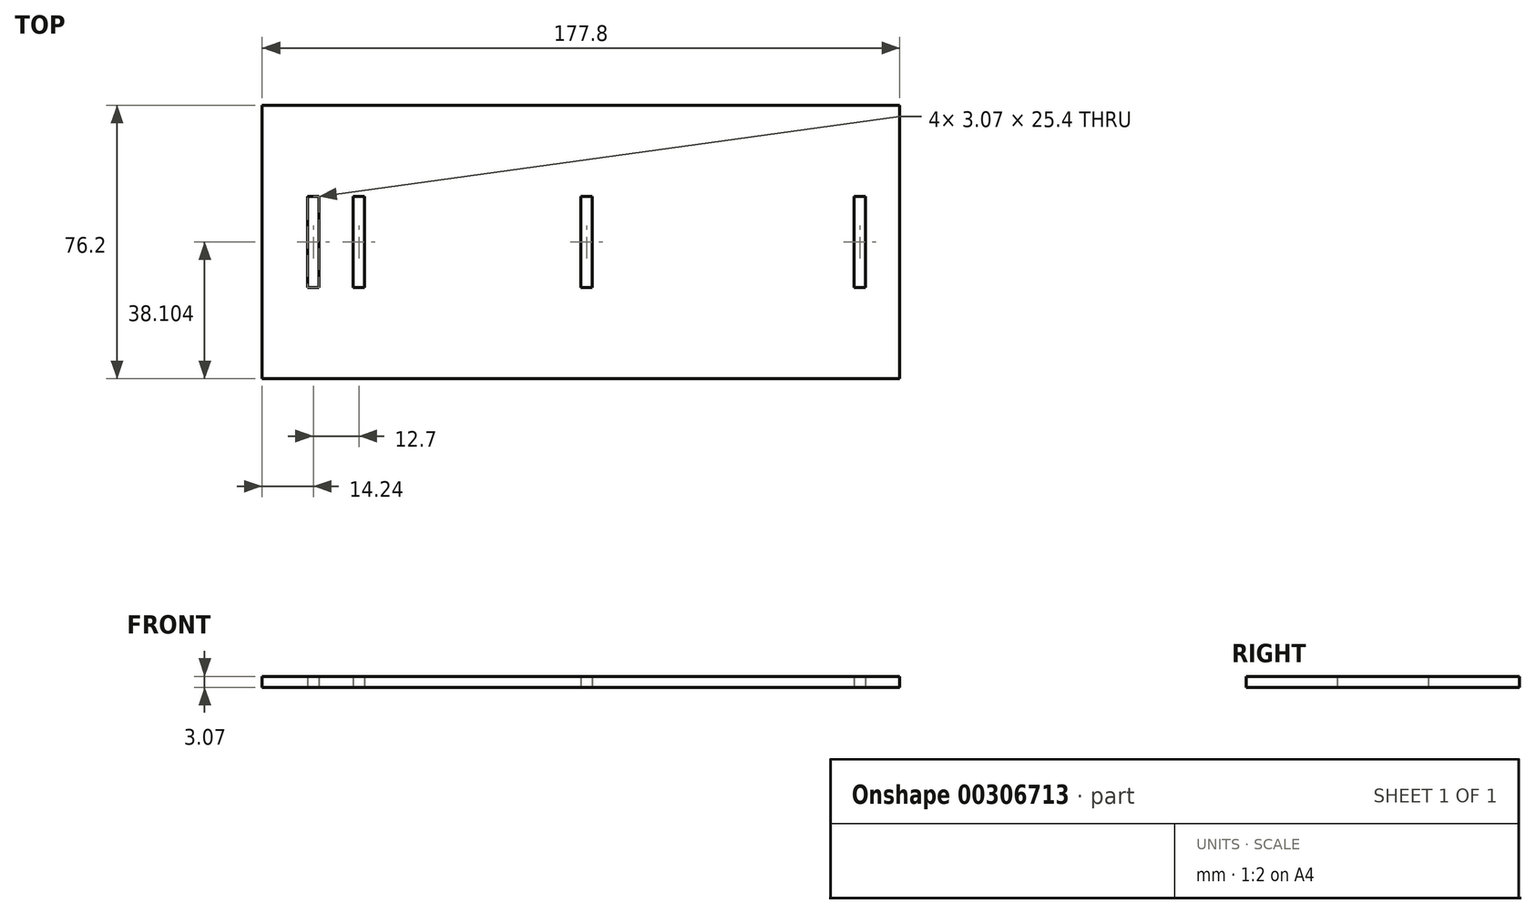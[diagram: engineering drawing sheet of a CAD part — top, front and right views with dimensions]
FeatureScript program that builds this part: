
annotation { "Feature Type Name" : "Feature", "Feature Type Description" : "" }
export const myFeature = defineFeature(function(context is Context, id is Id, definition is map)
    precondition{}
    {
        {
            var Q0;
            Q0=qCreatedBy(makeId("Top.planeOp"),FACE);
            var sketch = newSketch(context, id + "F0", { "sketchPlane" : qUnion([Q0])});
            skLineSegment(sketch, "E0.bottom", {"start": v(-70.59, 37.8) * mm, "end": v(107.21, 37.8) * mm});
            skLineSegment(sketch, "E0.top", {"start": v(-70.59, -38.4) * mm, "end": v(107.21, -38.4) * mm});
            skLineSegment(sketch, "E0.left", {"start": v(-70.59, 37.8) * mm, "end": v(-70.59, -38.4) * mm});
            skLineSegment(sketch, "E0.right", {"start": v(107.21, 37.8) * mm, "end": v(107.21, -38.4) * mm});
            skLineSegment(sketch, "E1.bottom", {"start": v(-57.89, 12.4) * mm, "end": v(-54.81, 12.4) * mm});
            skLineSegment(sketch, "E1.top", {"start": v(-57.89, -13) * mm, "end": v(-54.81, -13) * mm});
            skLineSegment(sketch, "E1.left", {"start": v(-57.89, 12.4) * mm, "end": v(-57.89, -13) * mm});
            skLineSegment(sketch, "E1.right", {"start": v(-54.81, 12.4) * mm, "end": v(-54.81, -13) * mm});
            skLineSegment(sketch, "E2.bottom", {"start": v(-45.19, 12.4) * mm, "end": v(-42.11, 12.4) * mm});
            skLineSegment(sketch, "E2.top", {"start": v(-45.19, -13) * mm, "end": v(-42.11, -13) * mm});
            skLineSegment(sketch, "E2.left", {"start": v(-45.19, 12.4) * mm, "end": v(-45.19, -13) * mm});
            skLineSegment(sketch, "E2.right", {"start": v(-42.11, 12.4) * mm, "end": v(-42.11, -13) * mm});
            skLineSegment(sketch, "E3.bottom", {"start": v(18.31, 12.4) * mm, "end": v(21.39, 12.4) * mm});
            skLineSegment(sketch, "E3.top", {"start": v(18.31, -13) * mm, "end": v(21.39, -13) * mm});
            skLineSegment(sketch, "E3.left", {"start": v(18.31, 12.4) * mm, "end": v(18.31, -13) * mm});
            skLineSegment(sketch, "E3.right", {"start": v(21.39, 12.4) * mm, "end": v(21.39, -13) * mm});
            skLineSegment(sketch, "E4.bottom", {"start": v(94.51, 12.4) * mm, "end": v(97.59, 12.4) * mm});
            skLineSegment(sketch, "E4.top", {"start": v(94.51, -13) * mm, "end": v(97.59, -13) * mm});
            skLineSegment(sketch, "E4.left", {"start": v(94.51, 12.4) * mm, "end": v(94.51, -13) * mm});
            skLineSegment(sketch, "E4.right", {"start": v(97.59, 12.4) * mm, "end": v(97.59, -13) * mm});
            skSolve(sketch);
        }
        {
            var Q0;
            Q0=makeQuery(id+"F0.imprint","IMPRINT",FACE,{"disambiguationData":[TD([[makeQuery(id+"F0.imprint","IMPRINT",EDGE,{"derivedFrom":sQuery(id+"F0.wireOp",EDGE,"E0.bottom")}),-1.0]])]});
            extrude(context, id + "F1", {"entities" : qUnion([Q0]), "depth" : 3.07 * mm});
        }
    });
